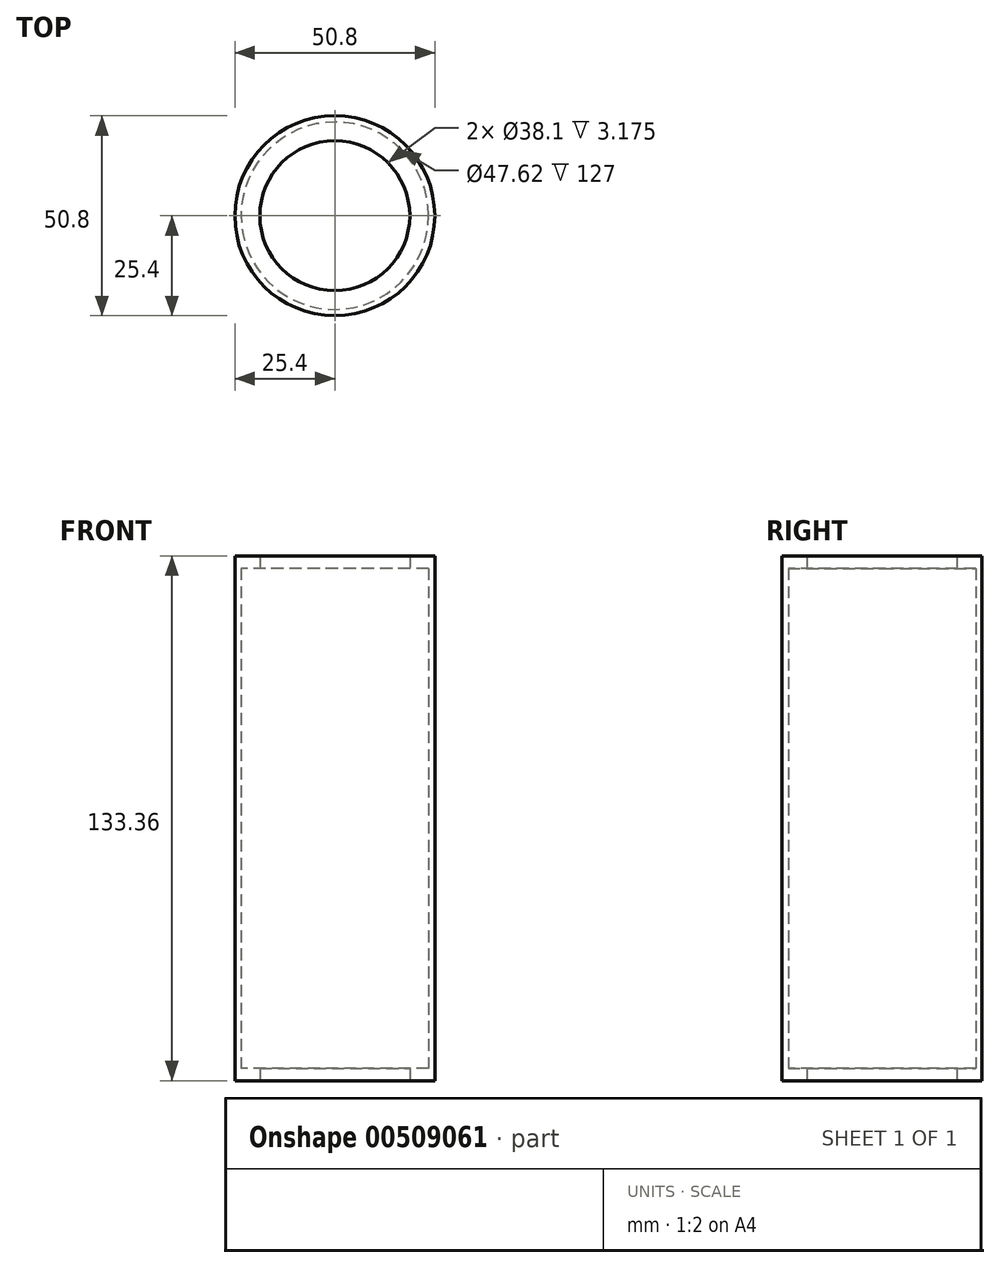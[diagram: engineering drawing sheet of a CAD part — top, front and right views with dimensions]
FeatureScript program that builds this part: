
annotation { "Feature Type Name" : "Feature", "Feature Type Description" : "" }
export const myFeature = defineFeature(function(context is Context, id is Id, definition is map)
    precondition{}
    {
        {
            var Q0;
            Q0=qCreatedBy(makeId("Top.planeOp"),FACE);
            var sketch = newSketch(context, id + "F0", { "sketchPlane" : qUnion([Q0])});
            skCircle(sketch, "E0", {"center": v(0, 0) * mm, "radius": 25.4 * mm});
            skCircle(sketch, "E1", {"center": v(0, 0) * mm, "radius": 23.81 * mm});
            skSolve(sketch);
        }
        {
            var Q0;
            Q0=makeQuery(id+"F0.imprint","IMPRINT",FACE,{"disambiguationData":[TD([[makeQuery(id+"F0.imprint","IMPRINT",EDGE,{"derivedFrom":sQuery(id+"F0.wireOp",EDGE,"E0")}),1.0]])]});
            extrude(context, id + "F1", {"entities" : qUnion([Q0]), "depth" : 127 * mm});
        }
        {
            var Q0;
            Q0=makeQuery(id+"F1.opExtrude","CAP_FACE",FACE,{"disambiguationData":[OSD([sQuery(id+"F0.wireOp",EDGE,"E0"),sQuery(id+"F0.wireOp",EDGE,"E1")])],"isStart":false});
            var sketch = newSketch(context, id + "F2", { "sketchPlane" : qUnion([Q0])});
            skCircle(sketch, "E2", {"center": v(0, 0) * mm, "radius": 25.4 * mm});
            skSolve(sketch);
        }
        {
            var Q0;
            Q0 = qSketchRegion(id + "F2", true);
            extrude(context, id + "F3", {"entities" : qUnion([Q0]), "operationType" : NewBodyOperationType.ADD, "depth" : 3.17 * mm});
        }
        {
            var Q0;
            Q0=makeQuery(id+"F1.opExtrude","CAP_FACE",FACE,{"disambiguationData":[OSD([sQuery(id+"F0.wireOp",EDGE,"E0"),sQuery(id+"F0.wireOp",EDGE,"E1")])],"isStart":true});
            var sketch = newSketch(context, id + "F4", { "sketchPlane" : qUnion([Q0])});
            skCircle(sketch, "E3", {"center": v(0, 0) * mm, "radius": 25.4 * mm});
            skSolve(sketch);
        }
        {
            var Q0;
            Q0 = qSketchRegion(id + "F4", true);
            extrude(context, id + "F5", {"entities" : qUnion([Q0]), "operationType" : NewBodyOperationType.ADD, "depth" : 3.17 * mm});
        }
        {
            var Q0;
            Q0=makeQuery(id+"F5.opExtrude","CAP_FACE",FACE,{"disambiguationData":[OSD([sQuery(id+"F4.wireOp",EDGE,"E3")])],"isStart":false});
            var sketch = newSketch(context, id + "F6", { "sketchPlane" : qUnion([Q0])});
            skCircle(sketch, "E4", {"center": v(0, 0) * mm, "radius": 19.05 * mm});
            skSolve(sketch);
        }
        {
            var Q0;
            Q0=sQuery(id+"F6.wireOp",VERTEX,"E4.center");
            var Q1;
            Q1=makeQuery(id+"F1.opExtrude","SWEPT_BODY",BODY,{"disambiguationData":[OSD([sQuery(id+"F0.wireOp",EDGE,"E0"),sQuery(id+"F0.wireOp",EDGE,"E1")])]});
            hole(context, id + "F7", {"style" : HoleStyle.SIMPLE, "endStyle" : HoleEndStyle.THROUGH, "holeDiameter" : 38.1 * mm, "isTappedThrough" : true, "tappedDepth" : 12.7 * mm, "tapClearance" : 3, "locations" : qUnion([Q0]), "scope" : qUnion([Q1])});
        }
    });
